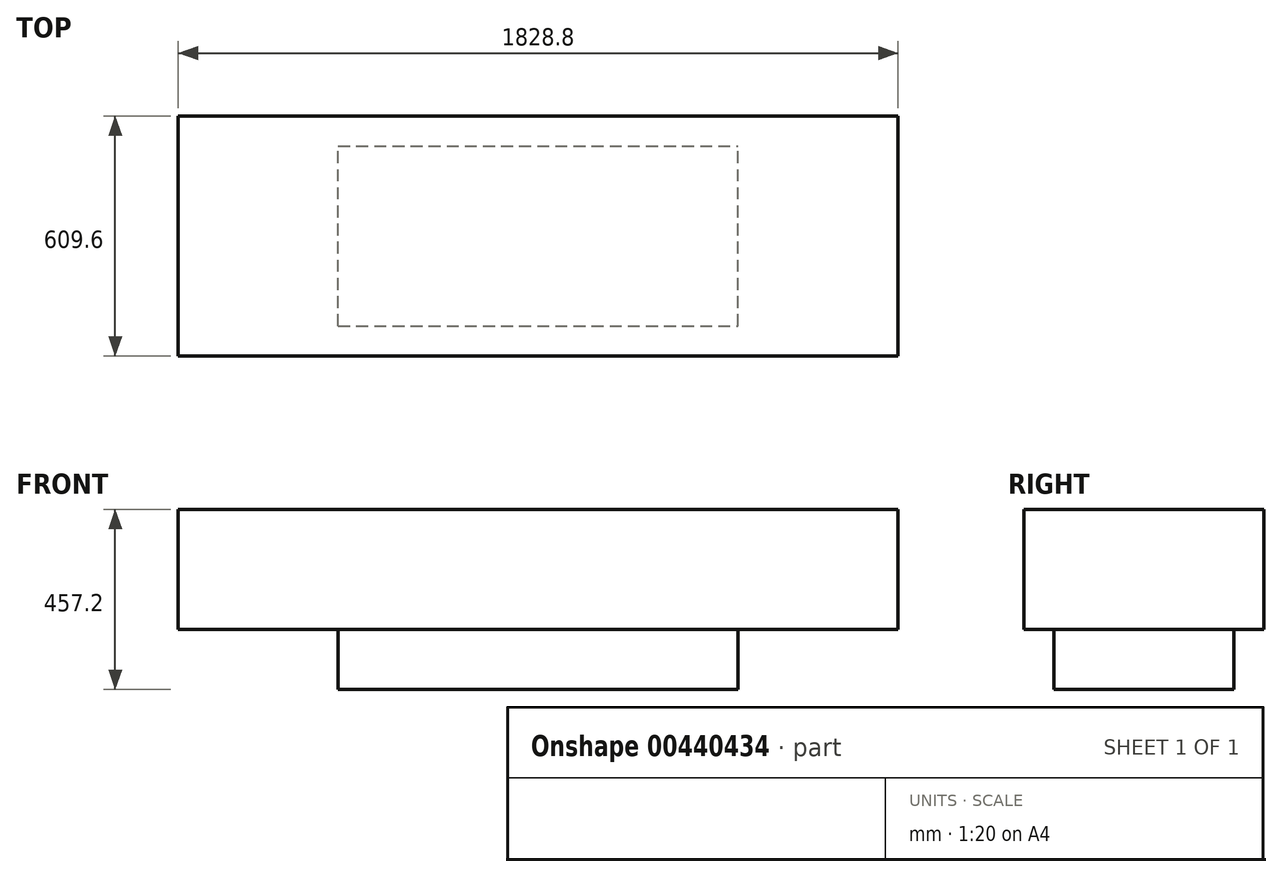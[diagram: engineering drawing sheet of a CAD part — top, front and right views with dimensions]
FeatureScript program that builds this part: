
annotation { "Feature Type Name" : "Feature", "Feature Type Description" : "" }
export const myFeature = defineFeature(function(context is Context, id is Id, definition is map)
    precondition{}
    {
        {
            var Q0;
            Q0=qCreatedBy(makeId("Front.planeOp"),FACE);
            var sketch = newSketch(context, id + "F0", { "sketchPlane" : qUnion([Q0])});
            skLineSegment(sketch, "E0.bottom", {"start": v(-508, -152.4) * mm, "end": v(508, -152.4) * mm});
            skLineSegment(sketch, "E0.left", {"start": v(-508, -152.4) * mm, "end": v(-508, 0) * mm});
            skLineSegment(sketch, "E0.right", {"start": v(508, -152.4) * mm, "end": v(508, 0) * mm});
            skLineSegment(sketch, "E1.bottom", {"start": v(-914.4, 304.8) * mm, "end": v(914.4, 304.8) * mm});
            skLineSegment(sketch, "E1.top", {"start": v(-914.4, 0) * mm, "end": v(914.4, 0) * mm});
            skLineSegment(sketch, "E1.left", {"start": v(-914.4, 304.8) * mm, "end": v(-914.4, 0) * mm});
            skLineSegment(sketch, "E1.right", {"start": v(914.4, 304.8) * mm, "end": v(914.4, 0) * mm});
            skLineSegment(sketch, "E2", {"start": v(0, 0) * mm, "end": v(0, -152.4) * mm});
            skSolve(sketch);
        }
        {
            var Q0;
            Q0=makeQuery(id+"F0.imprint","IMPRINT",FACE,{"disambiguationData":[TD([[makeQuery(id+"F0.imprint","IMPRINT",EDGE,{"derivedFrom":sQuery(id+"F0.wireOp",EDGE,"E1.bottom")}),-1.0]])]});
            extrude(context, id + "F1", {"entities" : qUnion([Q0]), "endBound" : BoundingType.SYMMETRIC, "depth" : 609.6 * mm});
        }
        {
            var Q0;
            {var subQ0=sQuery(id+"F0.wireOp",EDGE,"E0.left");Q0=makeQuery(id+"F0.imprint","IMPRINT",FACE,{"disambiguationData":[TD([[makeQuery(id+"F0.imprint","IMPRINT",EDGE,{"derivedFrom":subQ0}),-1.0]])]});}
            var Q1;
            {var subQ0=sQuery(id+"F0.wireOp",EDGE,"E0.right");Q1=makeQuery(id+"F0.imprint","IMPRINT",FACE,{"disambiguationData":[TD([[makeQuery(id+"F0.imprint","IMPRINT",EDGE,{"derivedFrom":subQ0}),1.0]])]});}
            extrude(context, id + "F2", {"entities" : qUnion([Q0, Q1]), "endBound" : BoundingType.SYMMETRIC, "depth" : 457.2 * mm});
        }
    });
